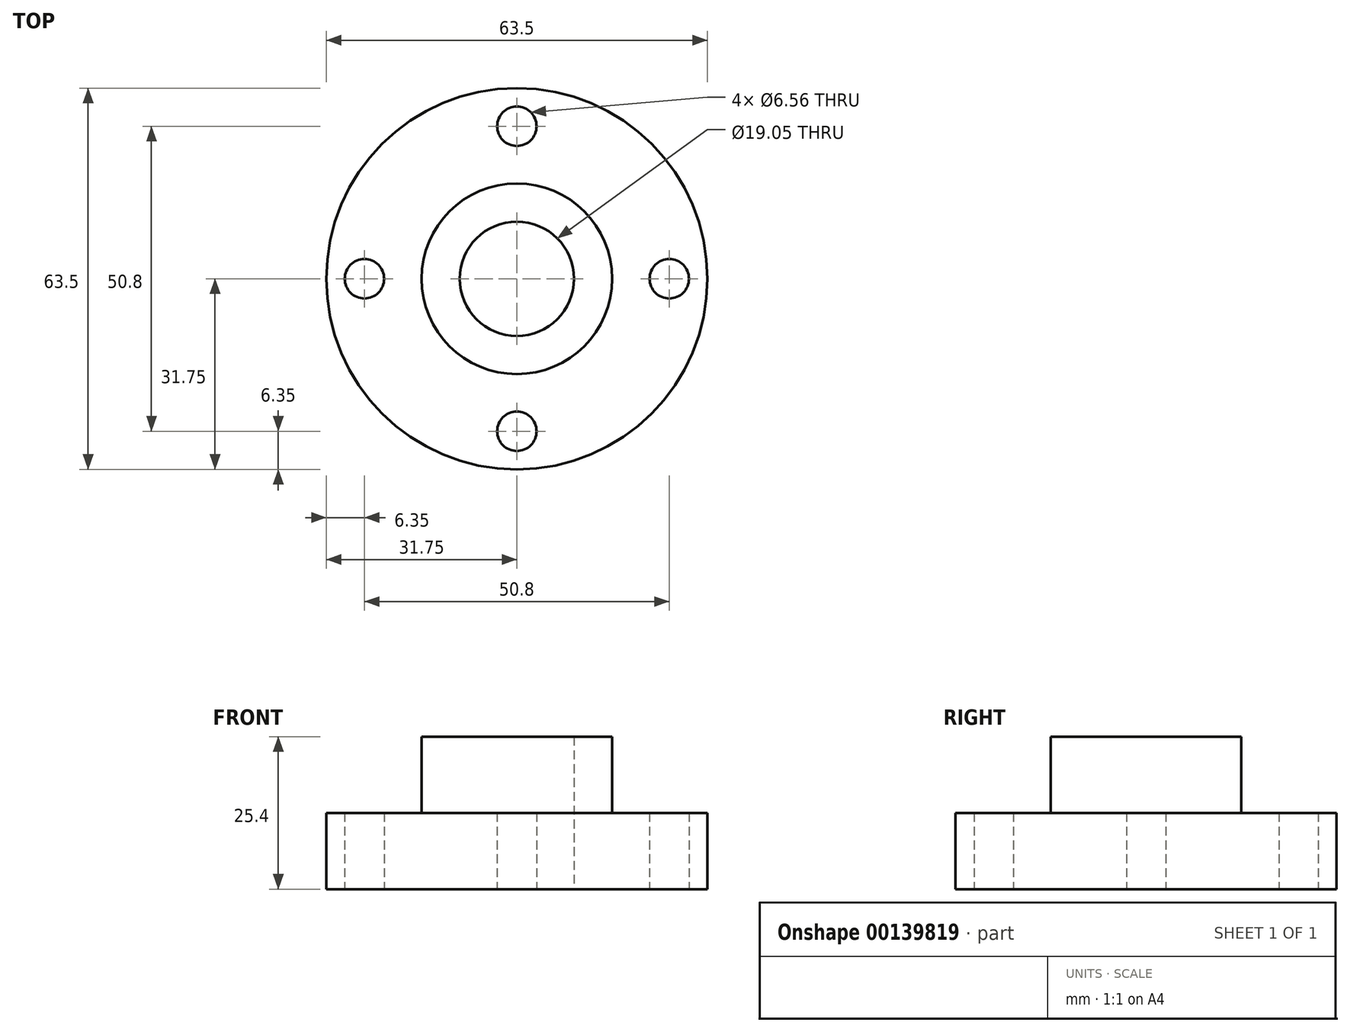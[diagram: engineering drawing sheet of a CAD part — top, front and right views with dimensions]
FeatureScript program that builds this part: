
annotation { "Feature Type Name" : "Feature", "Feature Type Description" : "" }
export const myFeature = defineFeature(function(context is Context, id is Id, definition is map)
    precondition{}
    {
        {
            var Q0;
            Q0=qCreatedBy(makeId("Top.planeOp"),FACE);
            var sketch = newSketch(context, id + "F0", { "sketchPlane" : qUnion([Q0])});
            skCircle(sketch, "E0", {"center": v(0, 0) * mm, "radius": 31.75 * mm});
            skCircle(sketch, "E1", {"center": v(0, 0) * mm, "radius": 15.88 * mm});
            skCircle(sketch, "E2", {"center": v(0, 0) * mm, "radius": 9.53 * mm});
            skCircle(sketch, "E3", {"center": v(0, 0) * mm, "radius": 25.4 * mm, "construction": true});
            skCircle(sketch, "E4", {"center": v(0, 25.4) * mm, "radius": 3.28 * mm});
            skCircle(sketch, "E5", {"center": v(-25.4, 0) * mm, "radius": 3.28 * mm});
            skCircle(sketch, "E6", {"center": v(0, -25.4) * mm, "radius": 3.28 * mm});
            skCircle(sketch, "E7", {"center": v(25.4, 0) * mm, "radius": 3.28 * mm});
            skSolve(sketch);
        }
        {
            var Q0;
            Q0 = qSketchRegion(id + "F0", true);
            var Q1;
            Q1=makeQuery(id+"F0.imprint","IMPRINT",FACE,{"disambiguationData":[TD([[makeQuery(id+"F0.imprint","IMPRINT",EDGE,{"derivedFrom":sQuery(id+"F0.wireOp",EDGE,"E1")}),1.0]])]});
            extrude(context, id + "F1", {"entities" : qUnion([Q0, Q1]), "depth" : 12.7 * mm});
        }
        {
            var Q0;
            Q0=makeQuery(id+"F0.imprint","IMPRINT",FACE,{"disambiguationData":[TD([[makeQuery(id+"F0.imprint","IMPRINT",EDGE,{"derivedFrom":sQuery(id+"F0.wireOp",EDGE,"E1")}),1.0]])]});
            extrude(context, id + "F2", {"entities" : qUnion([Q0]), "operationType" : NewBodyOperationType.ADD, "depth" : 25.4 * mm});
        }
    });
